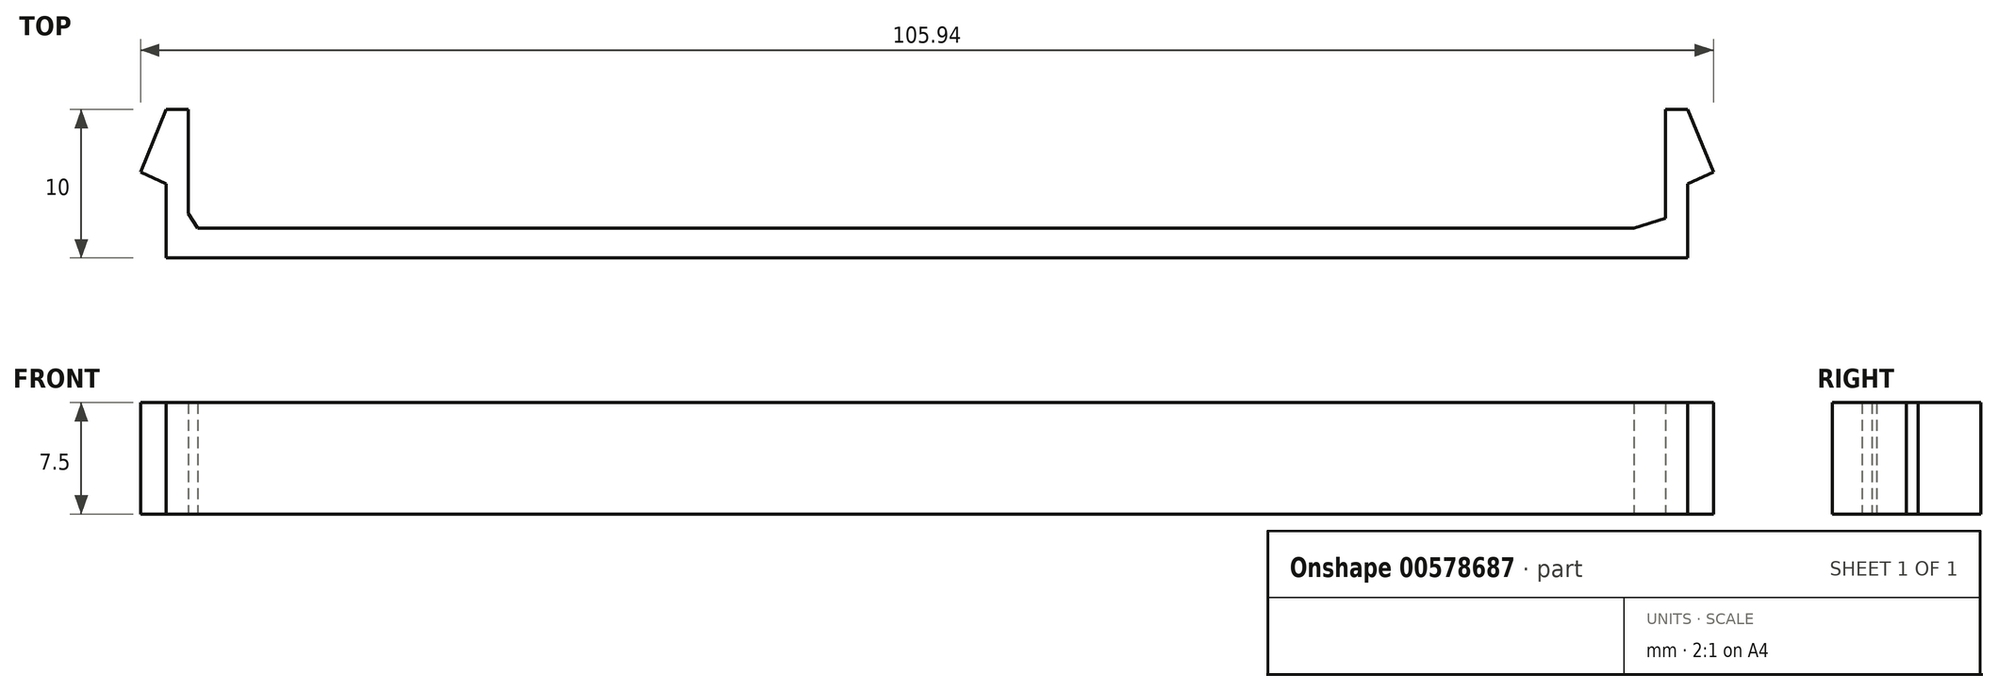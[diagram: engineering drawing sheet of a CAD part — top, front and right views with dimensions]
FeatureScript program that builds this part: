
annotation { "Feature Type Name" : "Feature", "Feature Type Description" : "" }
export const myFeature = defineFeature(function(context is Context, id is Id, definition is map)
    precondition{}
    {
        {
            var Q0;
            Q0=qCreatedBy(makeId("Top.planeOp"),FACE);
            var sketch = newSketch(context, id + "F0", { "sketchPlane" : qUnion([Q0])});
            skLineSegment(sketch, "E0.bottom", {"start": v(-52.49, 2) * mm, "end": v(50.01, 2) * mm});
            skLineSegment(sketch, "E0.top", {"start": v(-52.49, 0) * mm, "end": v(50.01, 0) * mm});
            skLineSegment(sketch, "E0.left", {"start": v(-52.49, 2) * mm, "end": v(-52.49, 0) * mm});
            skLineSegment(sketch, "E0.right", {"start": v(50.01, 2) * mm, "end": v(50.01, 0) * mm});
            skLineSegment(sketch, "E1", {"start": v(-52.49, 2) * mm, "end": v(-52.49, 10) * mm});
            skLineSegment(sketch, "E2", {"start": v(-52.49, 10) * mm, "end": v(-50.99, 10) * mm});
            skLineSegment(sketch, "E3", {"start": v(-50.99, 10) * mm, "end": v(-50.99, 2) * mm});
            skLineSegment(sketch, "E4", {"start": v(48.51, 2) * mm, "end": v(48.51, 10) * mm});
            skLineSegment(sketch, "E5", {"start": v(48.51, 10) * mm, "end": v(50.01, 10) * mm});
            skLineSegment(sketch, "E6", {"start": v(50.01, 10) * mm, "end": v(50.01, 2) * mm});
            skLineSegment(sketch, "E7", {"start": v(-52.49, 5) * mm, "end": v(-54.21, 5.8) * mm});
            skLineSegment(sketch, "E8", {"start": v(-54.21, 5.8) * mm, "end": v(-52.49, 10) * mm});
            skLineSegment(sketch, "E9", {"start": v(50.01, 5) * mm, "end": v(51.73, 5.8) * mm});
            skLineSegment(sketch, "E10", {"start": v(51.73, 5.8) * mm, "end": v(50.01, 10) * mm});
            skLineSegment(sketch, "E11", {"start": v(48.51, 2.67) * mm, "end": v(46.38, 2) * mm});
            skLineSegment(sketch, "E12", {"start": v(-50.99, 3) * mm, "end": v(-50.37, 2) * mm});
            skSolve(sketch);
        }
        {
            var Q0;
            Q0=makeQuery(id+"F0.imprint","IMPRINT",FACE,{"disambiguationData":[TD([[makeQuery(id+"F0.imprint","IMPRINT",EDGE,{"derivedFrom":sQuery(id+"F0.wireOp",EDGE,"E0.top")}),1.0]])]});
            var Q1;
            {var subQ0=sQuery(id+"F0.wireOp",EDGE,"E5");Q1=makeQuery(id+"F0.imprint","IMPRINT",FACE,{"disambiguationData":[TD([[makeQuery(id+"F0.imprint","IMPRINT",EDGE,{"derivedFrom":subQ0}),-1.0]])]});}
            var Q2;
            {var subQ3=sQuery(id+"F0.wireOp",EDGE,"E11");Q2=makeQuery(id+"F0.imprint","IMPRINT",FACE,{"disambiguationData":[TD([[makeQuery(id+"F0.imprint","IMPRINT",EDGE,{"derivedFrom":subQ3}),1.0]])]});}
            var Q3;
            {var subQ0=sQuery(id+"F0.wireOp",EDGE,"E2");Q3=makeQuery(id+"F0.imprint","IMPRINT",FACE,{"disambiguationData":[TD([[makeQuery(id+"F0.imprint","IMPRINT",EDGE,{"derivedFrom":subQ0}),-1.0]])]});}
            var Q4;
            {var subQ2=sQuery(id+"F0.wireOp",EDGE,"E9");Q4=makeQuery(id+"F0.imprint","IMPRINT",FACE,{"disambiguationData":[TD([[makeQuery(id+"F0.imprint","IMPRINT",EDGE,{"derivedFrom":subQ2}),1.0]])]});}
            var Q5;
            {var subQ2=sQuery(id+"F0.wireOp",EDGE,"E7");Q5=makeQuery(id+"F0.imprint","IMPRINT",FACE,{"disambiguationData":[TD([[makeQuery(id+"F0.imprint","IMPRINT",EDGE,{"derivedFrom":subQ2}),-1.0]])]});}
            var Q6;
            {var subQ3=sQuery(id+"F0.wireOp",EDGE,"E12");Q6=makeQuery(id+"F0.imprint","IMPRINT",FACE,{"disambiguationData":[TD([[makeQuery(id+"F0.imprint","IMPRINT",EDGE,{"derivedFrom":subQ3}),-1.0]])]});}
            extrude(context, id + "F1", {"entities" : qUnion([Q0, Q1, Q2, Q3, Q4, Q5, Q6]), "depth" : 7.5 * mm, "offsetDistance" : 25 * mm});
        }
    });
